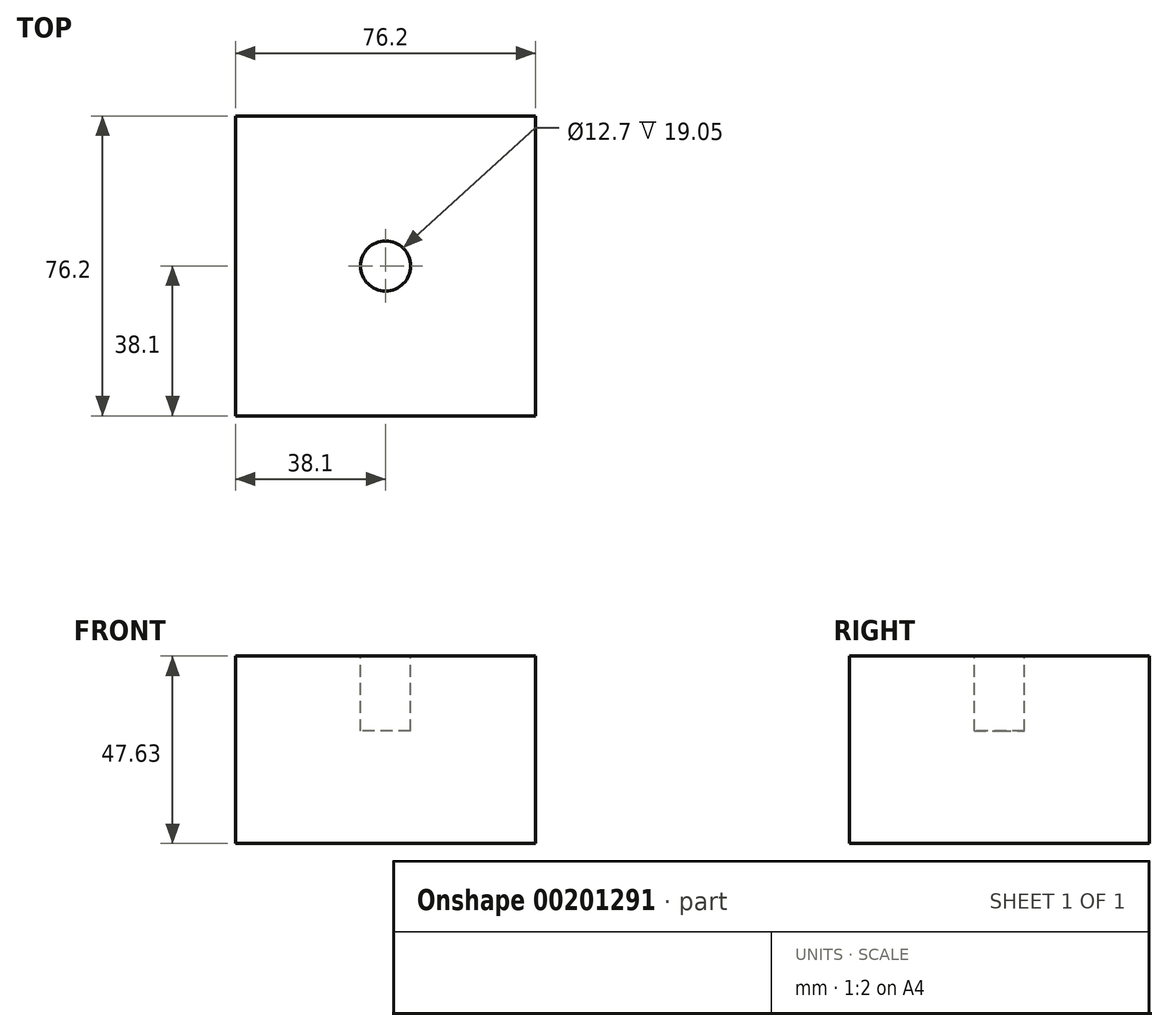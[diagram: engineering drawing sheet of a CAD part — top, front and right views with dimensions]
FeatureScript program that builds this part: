
annotation { "Feature Type Name" : "Feature", "Feature Type Description" : "" }
export const myFeature = defineFeature(function(context is Context, id is Id, definition is map)
    precondition{}
    {
        {
            var Q0;
            Q0=qCreatedBy(makeId("Top.planeOp"),FACE);
            var sketch = newSketch(context, id + "F0", { "sketchPlane" : qUnion([Q0])});
            skLineSegment(sketch, "E0.bottom", {"start": v(0, 0) * mm, "end": v(76.2, 0) * mm});
            skLineSegment(sketch, "E0.top", {"start": v(0, -76.2) * mm, "end": v(76.2, -76.2) * mm});
            skLineSegment(sketch, "E0.left", {"start": v(0, 0) * mm, "end": v(0, -76.2) * mm});
            skLineSegment(sketch, "E0.right", {"start": v(76.2, 0) * mm, "end": v(76.2, -76.2) * mm});
            skSolve(sketch);
        }
        {
            var Q0;
            Q0 = qSketchRegion(id + "F0", true);
            extrude(context, id + "F1", {"entities" : qUnion([Q0]), "depth" : 47.62 * mm});
        }
        {
            var Q0;
            Q0=makeQuery(id+"F1.opExtrude","CAP_FACE",FACE,{"disambiguationData":[OSD([sQuery(id+"F0.wireOp",EDGE,"E0.bottom"),sQuery(id+"F0.wireOp",EDGE,"E0.top"),sQuery(id+"F0.wireOp",EDGE,"E0.left"),sQuery(id+"F0.wireOp",EDGE,"E0.right")])],"isStart":false});
            var sketch = newSketch(context, id + "F2", { "sketchPlane" : qUnion([Q0])});
            skCircle(sketch, "E1", {"center": v(38.1, -38.1) * mm, "radius": 6.35 * mm});
            skPoint(sketch, "E1.centerSnap0", {"position": v(0, -38.1) * mm});
            skPoint(sketch, "E1.centerSnap1", {"position": v(38.1, 0) * mm});
            skSolve(sketch);
        }
        {
            var Q0;
            Q0 = qSketchRegion(id + "F2", true);
            extrude(context, id + "F3", {"entities" : qUnion([Q0]), "operationType" : NewBodyOperationType.REMOVE, "oppositeDirection" : true, "depth" : 19.05 * mm});
        }
    });
